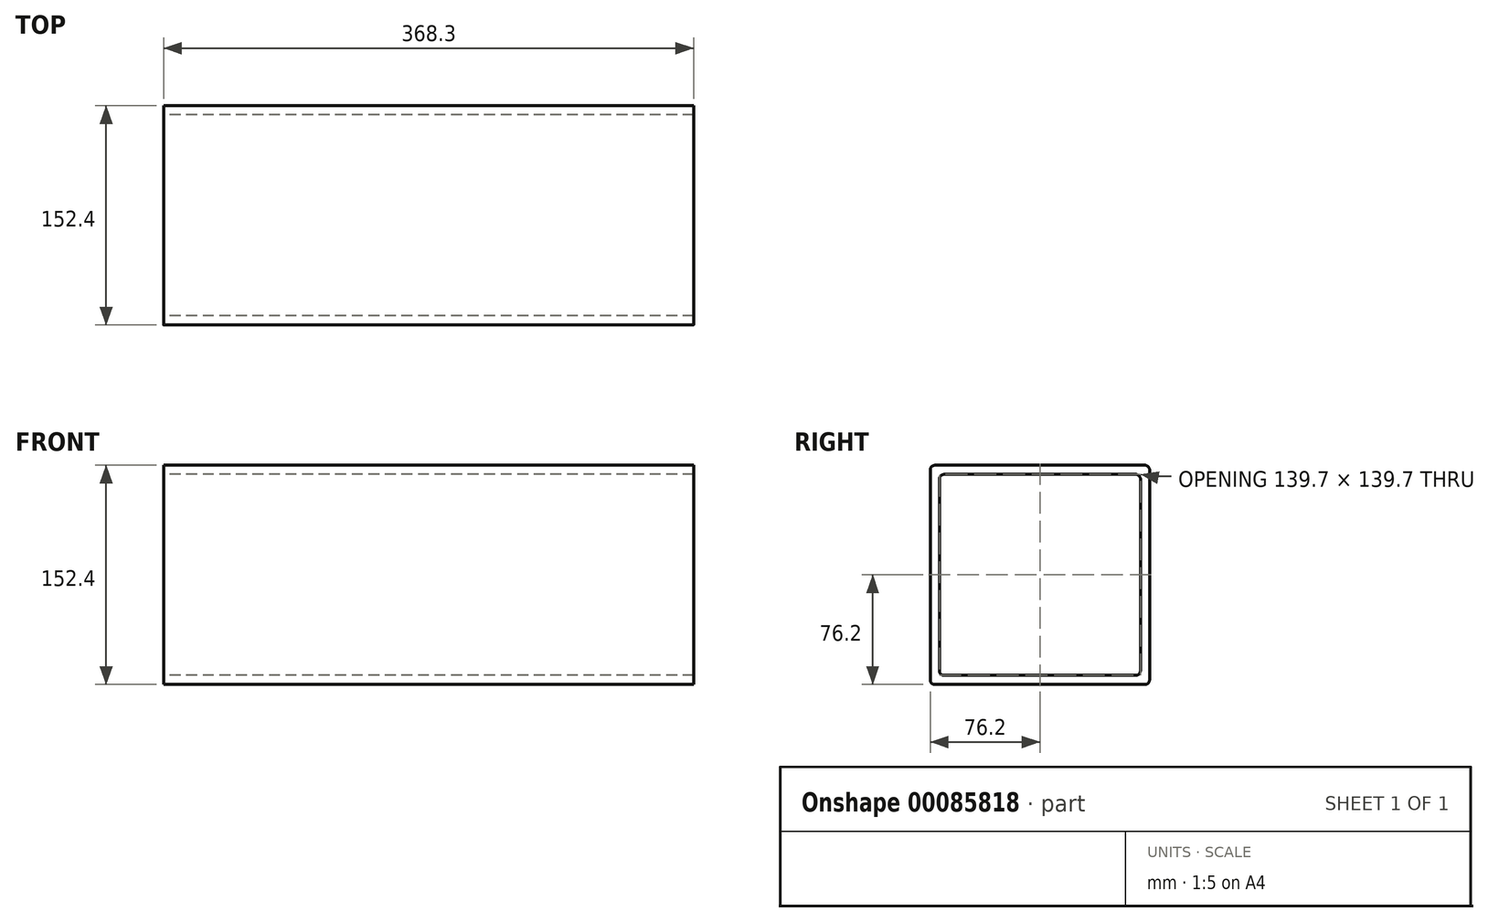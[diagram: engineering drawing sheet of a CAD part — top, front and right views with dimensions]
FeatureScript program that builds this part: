
annotation { "Feature Type Name" : "Feature", "Feature Type Description" : "" }
export const myFeature = defineFeature(function(context is Context, id is Id, definition is map)
    precondition{}
    {
        {
            var Q0;
            Q0=qCreatedBy(makeId("Right.planeOp"),FACE);
            var sketch = newSketch(context, id + "F0", { "sketchPlane" : qUnion([Q0])});
            skLineSegment(sketch, "E0.bottom", {"start": v(-73.03, 76.2) * mm, "end": v(73.03, 76.2) * mm});
            skLineSegment(sketch, "E0.top", {"start": v(-73.03, -76.2) * mm, "end": v(73.02, -76.2) * mm});
            skLineSegment(sketch, "E0.left", {"start": v(-76.2, 73.02) * mm, "end": v(-76.2, -73.03) * mm});
            skLineSegment(sketch, "E0.right", {"start": v(76.2, 73.02) * mm, "end": v(76.2, -73.03) * mm});
            skPoint(sketch, "E0.middle", {"position": v(0, 0) * mm});
            skLineSegment(sketch, "E1.0", {"start": v(-69.85, 66.68) * mm, "end": v(-69.85, -66.67) * mm});
            skLineSegment(sketch, "E2.3", {"start": v(-66.68, -69.85) * mm, "end": v(66.68, -69.85) * mm});
            skLineSegment(sketch, "E3.0", {"start": v(69.85, 66.68) * mm, "end": v(69.85, -66.67) * mm});
            skLineSegment(sketch, "E3.1", {"start": v(-66.68, 69.85) * mm, "end": v(66.68, 69.85) * mm});
            skPoint(sketch, "E4.visualSharp", {"position": v(-76.2, 76.2) * mm});
            skArc(sketch, "E4.filletArc", {"start": v(-73.03, 76.2) * mm, "mid": v(-75.27, 75.27) * mm, "end": v(-76.2, 73.02) * mm});
            skPoint(sketch, "E5.visualSharp", {"position": v(76.2, 76.2) * mm});
            skArc(sketch, "E5.filletArc", {"start": v(76.2, 73.02) * mm, "mid": v(75.27, 75.27) * mm, "end": v(73.03, 76.2) * mm});
            skPoint(sketch, "E6.visualSharp", {"position": v(76.2, -76.2) * mm});
            skArc(sketch, "E6.filletArc", {"start": v(73.02, -76.2) * mm, "mid": v(75.27, -75.27) * mm, "end": v(76.2, -73.03) * mm});
            skPoint(sketch, "E7.visualSharp", {"position": v(-76.2, -76.2) * mm});
            skArc(sketch, "E7.filletArc", {"start": v(-76.2, -73.03) * mm, "mid": v(-75.27, -75.27) * mm, "end": v(-73.03, -76.2) * mm});
            skPoint(sketch, "E8.visualSharp", {"position": v(-69.85, -69.85) * mm});
            skArc(sketch, "E8.filletArc", {"start": v(-69.85, -66.67) * mm, "mid": v(-68.92, -68.92) * mm, "end": v(-66.68, -69.85) * mm});
            skPoint(sketch, "E9.visualSharp", {"position": v(-69.85, 69.85) * mm});
            skArc(sketch, "E9.filletArc", {"start": v(-66.68, 69.85) * mm, "mid": v(-68.92, 68.92) * mm, "end": v(-69.85, 66.68) * mm});
            skPoint(sketch, "E10.visualSharp", {"position": v(69.85, 69.85) * mm});
            skArc(sketch, "E10.filletArc", {"start": v(69.85, 66.68) * mm, "mid": v(68.92, 68.92) * mm, "end": v(66.68, 69.85) * mm});
            skPoint(sketch, "E11.visualSharp", {"position": v(69.85, -69.85) * mm});
            skArc(sketch, "E11.filletArc", {"start": v(66.68, -69.85) * mm, "mid": v(68.92, -68.92) * mm, "end": v(69.85, -66.67) * mm});
            skSolve(sketch);
        }
        {
            var Q0;
            Q0=makeQuery(id+"F0.imprint","IMPRINT",FACE,{"disambiguationData":[TD([[makeQuery(id+"F0.imprint","IMPRINT",EDGE,{"derivedFrom":sQuery(id+"F0.wireOp",EDGE,"E0.bottom")}),-1.0]])]});
            extrude(context, id + "F1", {"entities" : qUnion([Q0]), "depth" : 368.3 * mm, "offsetDistance" : 25.4 * mm});
        }
    });
